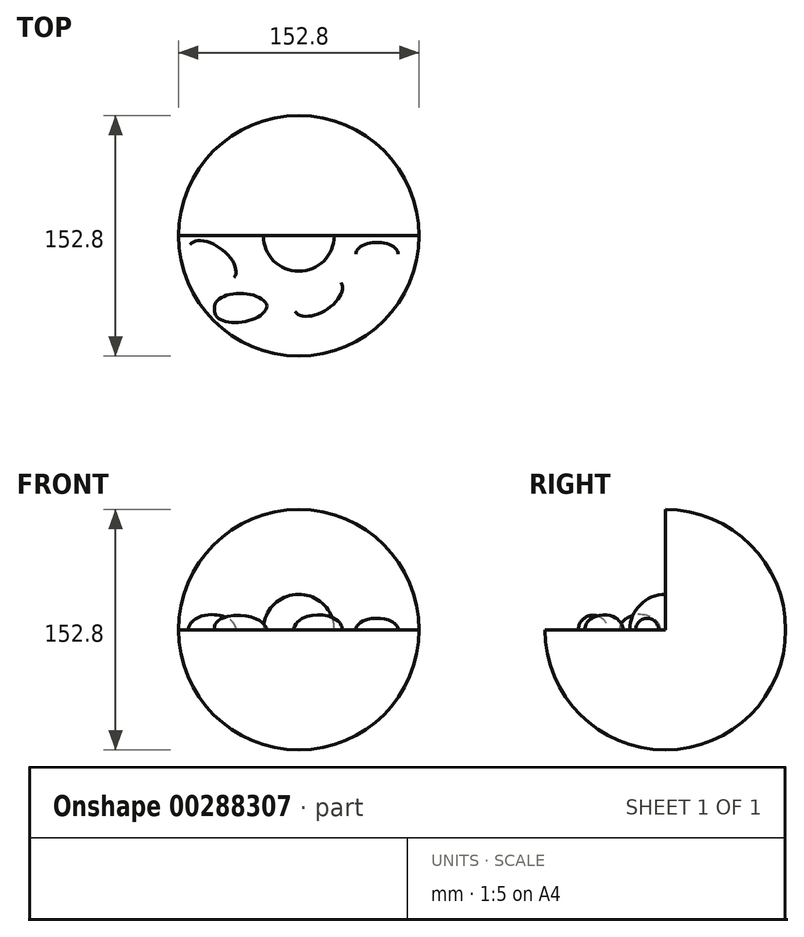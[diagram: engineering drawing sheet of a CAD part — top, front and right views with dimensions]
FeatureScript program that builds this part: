
annotation { "Feature Type Name" : "Feature", "Feature Type Description" : "" }
export const myFeature = defineFeature(function(context is Context, id is Id, definition is map)
    precondition{}
    {
        {
            var Q0;
            Q0=qCreatedBy(makeId("Front.planeOp"),FACE);
            var sketch = newSketch(context, id + "F0", { "sketchPlane" : qUnion([Q0])});
            skArc(sketch, "E0", {"start": v(76.4, 0) * mm, "mid": v(0, 76.4) * mm, "end": v(-76.4, 0) * mm});
            skLineSegment(sketch, "E1", {"start": v(-76.4, 0) * mm, "end": v(76.4, 0) * mm});
            skSolve(sketch);
        }
        {
            var Q0;
            Q0=makeQuery(id+"F0.imprint","IMPRINT",FACE,{"disambiguationData":[TD([[makeQuery(id+"F0.imprint","IMPRINT",EDGE,{"derivedFrom":sQuery(id+"F0.wireOp",EDGE,"E0")}),1.0]])]});
            var Q1;
            Q1=sQuery(id+"F0.wireOp",EDGE,"E1");
            revolve(context, id + "F1", {"entities" : qUnion([Q0]), "axis" : qUnion([Q1]), "revolveType" : RevolveType.ONE_DIRECTION, "oppositeDirection" : true, "angle" : 270 * degree});
        }
        {
            var Q0;
            Q0=makeQuery(id+"F1.opRevolve","CAP_FACE",FACE,{"disambiguationData":[OSD([sQuery(id+"F0.wireOp",EDGE,"E0"),sQuery(id+"F0.wireOp",EDGE,"E1")])],"isStart":true});
            var sketch = newSketch(context, id + "F2", { "sketchPlane" : qUnion([Q0])});
            skArc(sketch, "E2", {"start": v(22.53, 0) * mm, "mid": v(0, 22.53) * mm, "end": v(-22.53, 0) * mm});
            skLineSegment(sketch, "E3", {"start": v(-22.53, 0) * mm, "end": v(22.53, 0) * mm});
            skSolve(sketch);
        }
        {
            var Q0;
            Q0=makeQuery(id+"F2.imprint","IMPRINT",FACE,{"disambiguationData":[TD([[makeQuery(id+"F2.imprint","IMPRINT",EDGE,{"derivedFrom":sQuery(id+"F2.wireOp",EDGE,"E2")}),1.0]])]});
            var Q1;
            Q1=sQuery(id+"F2.wireOp",EDGE,"E3");
            revolve(context, id + "F3", {"entities" : qUnion([Q0]), "axis" : qUnion([Q1]), "revolveType" : RevolveType.ONE_DIRECTION, "angle" : 90 * degree});
        }
        {
            var Q0;
            Q0=makeQuery(id+"F1.opRevolve","CAP_FACE",FACE,{"disambiguationData":[OSD([sQuery(id+"F0.wireOp",EDGE,"E0"),sQuery(id+"F0.wireOp",EDGE,"E1")])],"isStart":false});
            var sketch = newSketch(context, id + "F4", { "sketchPlane" : qUnion([Q0])});
            skEllipticalArc(sketch, "E4", {});
            skEllipticalArc(sketch, "E5", {});
            skEllipticalArc(sketch, "E6", {});
            skEllipticalArc(sketch, "E7", {});
            skLineSegment(sketch, "E8", {"start": v(-69.05, -5.65) * mm, "end": v(-41.05, -26.65) * mm});
            skLineSegment(sketch, "E9", {"start": v(-53.43, -46.95) * mm, "end": v(-20.05, -44.57) * mm});
            skPoint(sketch, "E9.startSnap0", {"position": v(-53.43, -48.72) * mm});
            skPoint(sketch, "E9.endSnap0", {"position": v(-20.05, -42.8) * mm});
            skLineSegment(sketch, "E10", {"start": v(26.78, -29.88) * mm, "end": v(-2.29, -48.18) * mm});
            skLineSegment(sketch, "E11", {"start": v(36.2, -11.57) * mm, "end": v(63.12, -11.57) * mm});
            const initialGuessF4  = {"E4": [0.012247901409864426, -0.03903178125619888, -0.8462328020623665, -0.5328133300825683, 0.017177269762905033, 0.009499380093357539, 0, 3.141592653589793], "E5": [0.04966457560658455, -0.011574942618608475, -1, 0, 0.013459235429763794, 0.00729135716965938, 3.141592653589793, 0], "E6": [-0.055048272013664246, -0.016151081770658493, 0.8000000510984303, -0.5999999318687536, 0.017497007548809115, 0.009621355986971019, 0, 3.141592653589793], "E7": [-0.036743711680173874, -0.04576139897108078, 0.9846232620833943, 0.17469124695947227, 0.016950088479580246, 0.009162928059472051, 2.9503578275164726, 0]};
            skSetInitialGuess(sketch, initialGuessF4);
            skSolve(sketch);
        }
        {
            var Q0;
            Q0=makeQuery(id+"F4.imprint","IMPRINT",FACE,{"disambiguationData":[TD([[makeQuery(id+"F4.imprint","IMPRINT",EDGE,{"derivedFrom":sQuery(id+"F4.wireOp",EDGE,"E6")}),1.0]])]});
            var Q1;
            Q1=sQuery(id+"F4.wireOp",EDGE,"E8");
            revolve(context, id + "F5", {"entities" : qUnion([Q0]), "axis" : qUnion([Q1]), "revolveType" : RevolveType.ONE_DIRECTION, "angle" : 180 * degree});
        }
        {
            var Q0;
            {var subQ0=sQuery(id+"F4.wireOp",EDGE,"E9");Q0=makeQuery(id+"F4.imprint","IMPRINT",FACE,{"disambiguationData":[TD([[makeQuery(id+"F4.imprint","IMPRINT",EDGE,{"derivedFrom":subQ0}),-1.0]])]});}
            var Q1;
            Q1=sQuery(id+"F4.wireOp",EDGE,"E9");
            revolve(context, id + "F6", {"entities" : qUnion([Q0]), "axis" : qUnion([Q1]), "revolveType" : RevolveType.ONE_DIRECTION, "oppositeDirection" : true, "angle" : 180 * degree});
        }
        {
            var Q0;
            Q0=makeQuery(id+"F4.imprint","IMPRINT",FACE,{"disambiguationData":[TD([[makeQuery(id+"F4.imprint","IMPRINT",EDGE,{"derivedFrom":sQuery(id+"F4.wireOp",EDGE,"E4")}),1.0]])]});
            var Q1;
            Q1=sQuery(id+"F4.wireOp",EDGE,"E10");
            revolve(context, id + "F7", {"entities" : qUnion([Q0]), "axis" : qUnion([Q1]), "revolveType" : RevolveType.ONE_DIRECTION, "angle" : 180 * degree});
        }
        {
            var Q0;
            Q0=makeQuery(id+"F4.imprint","IMPRINT",FACE,{"disambiguationData":[TD([[makeQuery(id+"F4.imprint","IMPRINT",EDGE,{"derivedFrom":sQuery(id+"F4.wireOp",EDGE,"E5")}),1.0]])]});
            var Q1;
            Q1=sQuery(id+"F4.wireOp",EDGE,"E11");
            revolve(context, id + "F8", {"entities" : qUnion([Q0]), "axis" : qUnion([Q1]), "revolveType" : RevolveType.ONE_DIRECTION, "angle" : 180 * degree});
        }
    });
